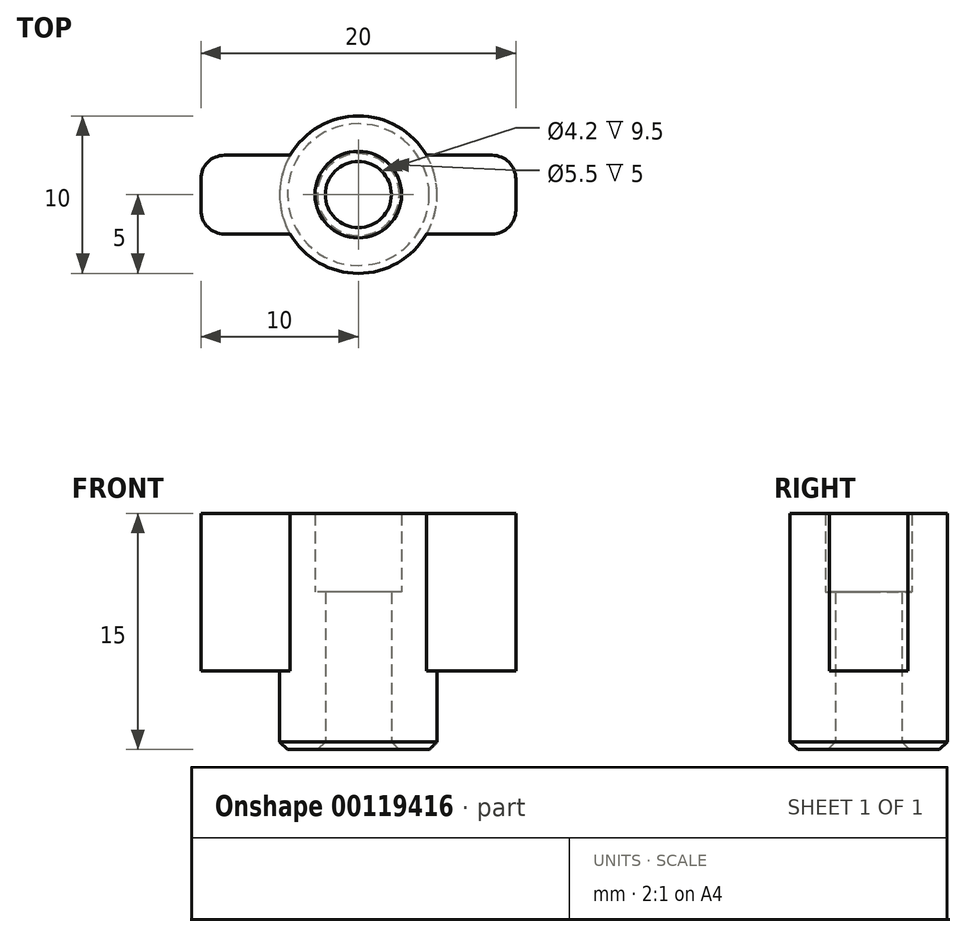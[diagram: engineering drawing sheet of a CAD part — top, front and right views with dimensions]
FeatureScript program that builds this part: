
annotation { "Feature Type Name" : "Feature", "Feature Type Description" : "" }
export const myFeature = defineFeature(function(context is Context, id is Id, definition is map)
    precondition{}
    {
        {
            var Q0;
            Q0=qCreatedBy(makeId("Top.planeOp"),FACE);
            var sketch = newSketch(context, id + "F0", { "sketchPlane" : qUnion([Q0])});
            skCircle(sketch, "E0", {"center": v(0, 0) * mm, "radius": 2.1 * mm});
            skCircle(sketch, "E1", {"center": v(0, 0) * mm, "radius": 5 * mm});
            skSolve(sketch);
        }
        {
            var Q0;
            Q0=makeQuery(id+"F0.imprint","IMPRINT",FACE,{"disambiguationData":[TD([[makeQuery(id+"F0.imprint","IMPRINT",EDGE,{"derivedFrom":sQuery(id+"F0.wireOp",EDGE,"E0")}),-1.0]])]});
            extrude(context, id + "F1", {"entities" : qUnion([Q0]), "depth" : 10 * mm});
        }
        {
            var Q0;
            Q0=makeQuery(id+"F1.opExtrude","CAP_FACE",FACE,{"disambiguationData":[OSD([sQuery(id+"F0.wireOp",EDGE,"E0"),sQuery(id+"F0.wireOp",EDGE,"E1")])],"isStart":false});
            var sketch = newSketch(context, id + "F2", { "sketchPlane" : qUnion([Q0])});
            skCircle(sketch, "E2", {"center": v(0, 0) * mm, "radius": 2.75 * mm});
            skArc(sketch, "E3", {"start": v(4.33, 2.5) * mm, "mid": v(0, 5) * mm, "end": v(-4.33, 2.5) * mm});
            skLineSegment(sketch, "E4.bottom", {"start": v(8.5, -2.5) * mm, "end": v(4.33, -2.5) * mm});
            skLineSegment(sketch, "E4.top", {"start": v(8.5, 2.5) * mm, "end": v(4.33, 2.5) * mm});
            skLineSegment(sketch, "E4.left", {"start": v(10, -1) * mm, "end": v(10, 1) * mm});
            skLineSegment(sketch, "E4.right", {"start": v(-10, -1) * mm, "end": v(-10, 1) * mm});
            skLineSegment(sketch, "E5.trimOffspring", {"start": v(-4.33, 2.5) * mm, "end": v(-8.5, 2.5) * mm});
            skLineSegment(sketch, "E6.trimOffspring", {"start": v(-4.33, -2.5) * mm, "end": v(-8.5, -2.5) * mm});
            skArc(sketch, "E7.trimOffspring", {"start": v(-4.33, -2.5) * mm, "mid": v(0, -5) * mm, "end": v(4.33, -2.5) * mm});
            skPoint(sketch, "E8.visualSharp", {"position": v(-10, 2.5) * mm});
            skArc(sketch, "E8.filletArc", {"start": v(-8.5, 2.5) * mm, "mid": v(-9.56, 2.06) * mm, "end": v(-10, 1) * mm});
            skPoint(sketch, "E9.visualSharp", {"position": v(10, 2.5) * mm});
            skArc(sketch, "E9.filletArc", {"start": v(10, 1) * mm, "mid": v(9.56, 2.06) * mm, "end": v(8.5, 2.5) * mm});
            skPoint(sketch, "E10.visualSharp", {"position": v(10, -2.5) * mm});
            skArc(sketch, "E10.filletArc", {"start": v(8.5, -2.5) * mm, "mid": v(9.56, -2.06) * mm, "end": v(10, -1) * mm});
            skPoint(sketch, "E11.visualSharp", {"position": v(-10, -2.5) * mm});
            skArc(sketch, "E11.filletArc", {"start": v(-10, -1) * mm, "mid": v(-9.56, -2.06) * mm, "end": v(-8.5, -2.5) * mm});
            skSolve(sketch);
        }
        {
            var Q0;
            Q0=makeQuery(id+"F2.imprint","IMPRINT",FACE,{"disambiguationData":[TD([[makeQuery(id+"F2.imprint","IMPRINT",EDGE,{"derivedFrom":sQuery(id+"F2.wireOp",EDGE,"E2")}),-1.0]])]});
            var Q1;
            {var subQ1=sQuery(id+"F2.wireOp",EDGE,"E4.bottom");Q1=makeQuery(id+"F2.imprint","IMPRINT",FACE,{"disambiguationData":[TD([[makeQuery(id+"F2.imprint","IMPRINT",EDGE,{"derivedFrom":subQ1}),-1.0]])]});}
            var Q2;
            Q2=makeQuery(id+"F2.imprint","IMPRINT",FACE,{"disambiguationData":[TD([[makeQuery(id+"F2.imprint","IMPRINT",EDGE,{"derivedFrom":sQuery(id+"F2.wireOp",EDGE,"E4.right")}),-1.0]])]});
            extrude(context, id + "F3", {"entities" : qUnion([Q0, Q1, Q2]), "operationType" : NewBodyOperationType.ADD, "endBound" : BoundingType.SYMMETRIC, "depth" : 10 * mm});
        }
        {
            var Q0;
            Q0=makeQuery(id+"F1.opExtrude","CAP_EDGE",EDGE,{"disambiguationData":[OSD([sQuery(id+"F0.wireOp",EDGE,"E1")])],"isStart":true});
            var Q1;
            Q1=makeQuery(id+"F1.opExtrude","CAP_EDGE",EDGE,{"disambiguationData":[OSD([sQuery(id+"F0.wireOp",EDGE,"E0")])],"isStart":true});
            chamfer(context, id + "F4", {"entities" : qUnion([Q0, Q1]), "width" : .5 * mm, "tangentPropagation" : true});
        }
    });
